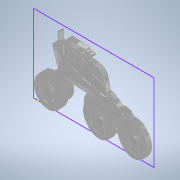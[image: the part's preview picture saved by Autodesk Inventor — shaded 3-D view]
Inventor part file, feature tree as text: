
AUTODESK INVENTOR PART (.ipt)
format: ipt  version: 2020.1 (Build 241239000, 239)  size: 2,402,304 bytes
history: native  units: mm
features: other x2, sketch x1
ambient origin geometry x8: Origin, YZ Plane, XZ Plane, XY Plane, X Axis, Y Axis, Z Axis, Center Point
feature tree (3):
  other  "Rover 3 - Verde"
  sketch  "Boceto1"
  other  "MeshFeature1"
